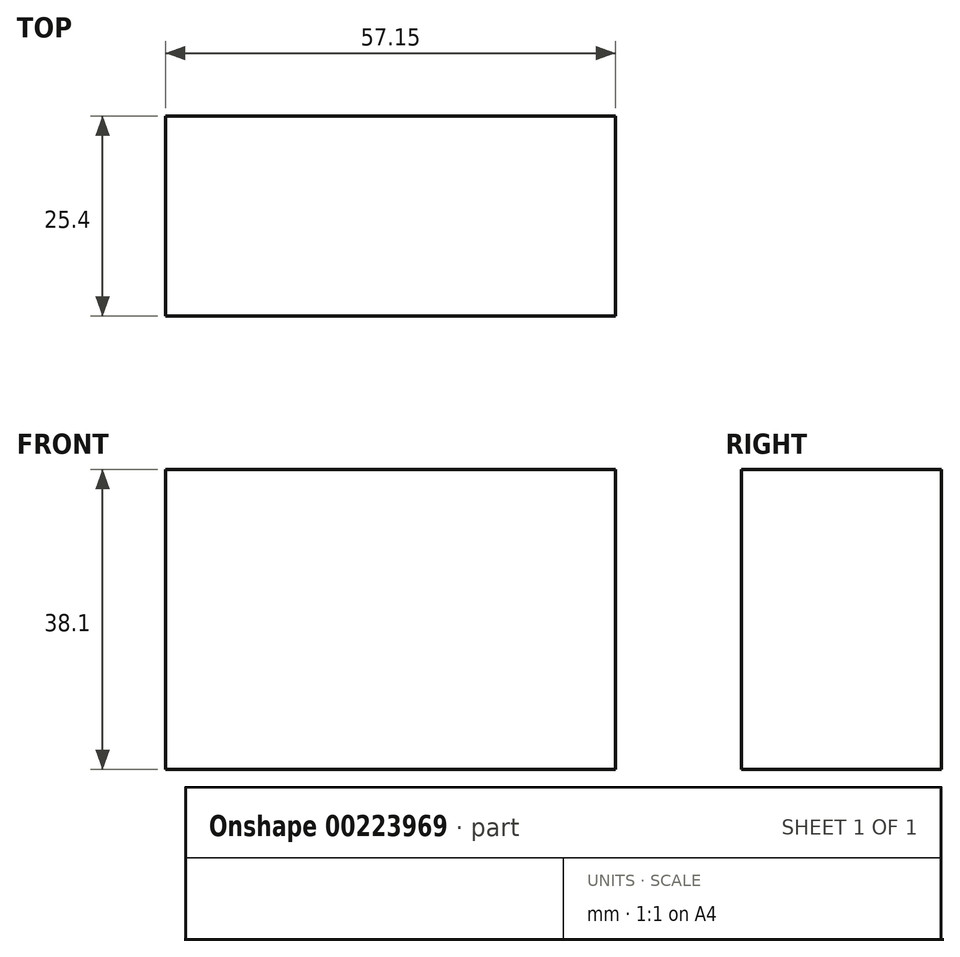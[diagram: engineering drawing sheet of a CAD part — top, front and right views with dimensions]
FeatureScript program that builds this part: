
annotation { "Feature Type Name" : "Feature", "Feature Type Description" : "" }
export const myFeature = defineFeature(function(context is Context, id is Id, definition is map)
    precondition{}
    {
        {
            var Q0;
            Q0=qCreatedBy(makeId("Front.planeOp"),FACE);
            var sketch = newSketch(context, id + "F0", { "sketchPlane" : qUnion([Q0])});
            skLineSegment(sketch, "E0.bottom", {"start": v(-39.4, 23.3) * mm, "end": v(-96.55, 23.3) * mm});
            skLineSegment(sketch, "E0.top", {"start": v(-39.4, 61.4) * mm, "end": v(-96.55, 61.4) * mm});
            skLineSegment(sketch, "E0.left", {"start": v(-39.4, 23.3) * mm, "end": v(-39.4, 61.4) * mm});
            skLineSegment(sketch, "E0.right", {"start": v(-96.55, 23.3) * mm, "end": v(-96.55, 61.4) * mm});
            skPoint(sketch, "E0.middle", {"position": v(-67.97, 42.34) * mm});
            skSolve(sketch);
        }
        {
            var Q0;
            Q0=qSketchRegion(id+"F0",true);
            extrude(context, id + "F1", {"entities" : qUnion([Q0]), "endBound" : BoundingType.SYMMETRIC, "depth" : 25.4 * mm});
        }
    });
